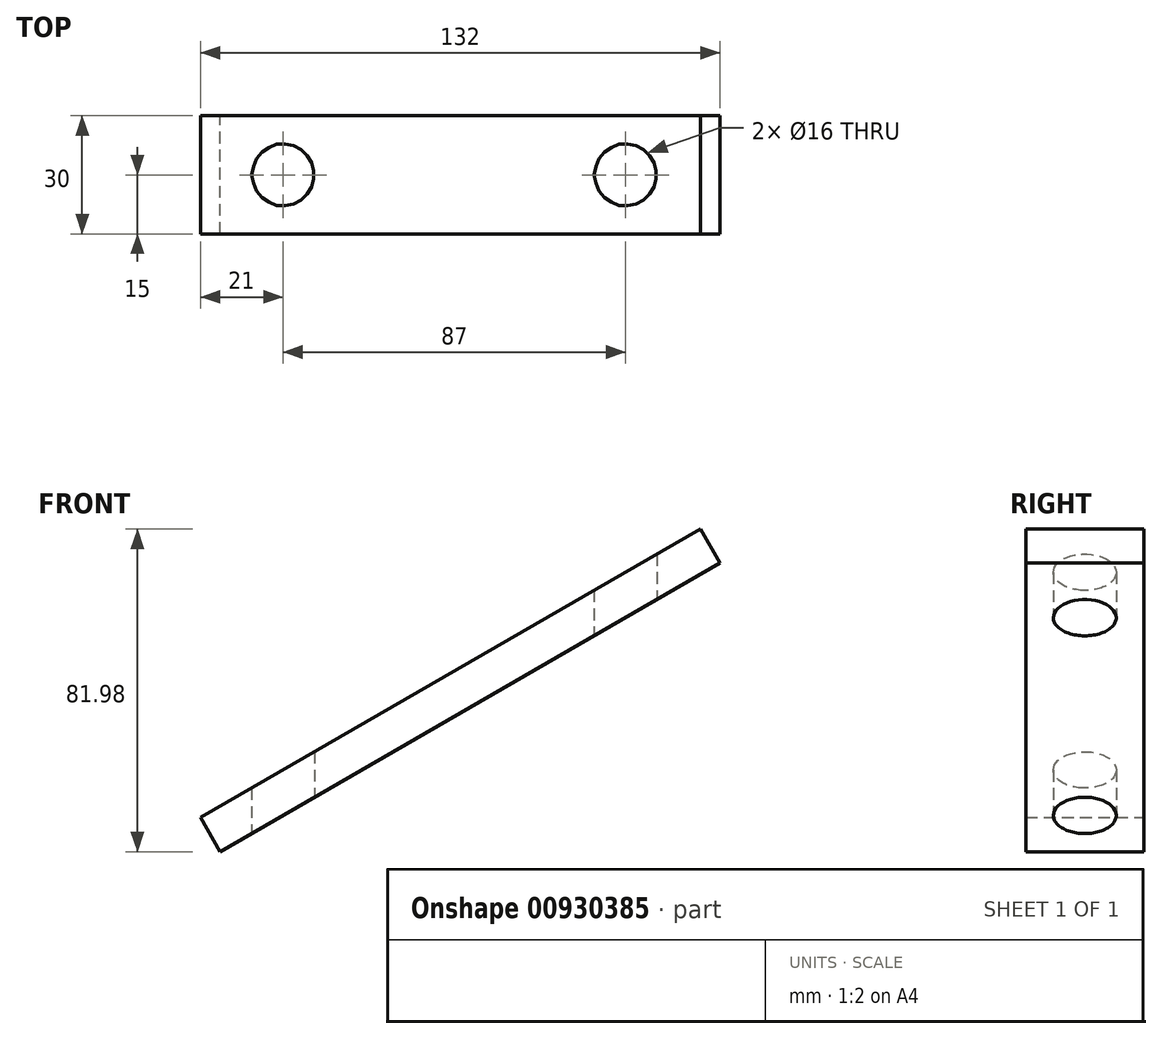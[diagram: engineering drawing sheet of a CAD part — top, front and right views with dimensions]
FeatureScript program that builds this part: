
annotation { "Feature Type Name" : "Feature", "Feature Type Description" : "" }
export const myFeature = defineFeature(function(context is Context, id is Id, definition is map)
    precondition{}
    {
        {
            var Q0;
            Q0=qCreatedBy(makeId("Top.planeOp"),FACE);
            var sketch = newSketch(context, id + "F0", { "sketchPlane" : qUnion([Q0])});
            skCircle(sketch, "E0", {"center": v(16, 0) * mm, "radius": 8 * mm});
            skCircle(sketch, "E1.1.0.0", {"center": v(103, 0) * mm, "radius": 8 * mm});
            skLineSegment(sketch, "E1.direction1", {"start": v(16, 0) * mm, "end": v(103, 0) * mm, "construction": true});
            skSolve(sketch);
        }
        {
            var Q0;
            Q0=qCreatedBy(makeId("Front.planeOp"),FACE);
            var sketch = newSketch(context, id + "F1", { "sketchPlane" : qUnion([Q0])});
            skLineSegment(sketch, "E2.bottom", {"start": v(-5, 8.66) * mm, "end": v(122, 81.98) * mm});
            skLineSegment(sketch, "E2.top", {"start": v(0, 0) * mm, "end": v(127, 73.32) * mm});
            skLineSegment(sketch, "E2.left", {"start": v(-5, 8.66) * mm, "end": v(0, 0) * mm});
            skLineSegment(sketch, "E2.right", {"start": v(122, 81.98) * mm, "end": v(127, 73.32) * mm});
            skLineSegment(sketch, "E3", {"start": v(103, 0) * mm, "end": v(103, 76.59) * mm, "construction": true});
            skSolve(sketch);
        }
        {
            var Q0;
            Q0 = qSketchRegion(id + "F1", true);
            extrude(context, id + "F2", {"entities" : qUnion([Q0]), "endBound" : BoundingType.SYMMETRIC, "depth" : 30 * mm, "offsetDistance" : 25 * mm});
        }
        {
            var Q0;
            Q0 = qSketchRegion(id + "F0", true);
            extrude(context, id + "F3", {"entities" : qUnion([Q0]), "operationType" : NewBodyOperationType.REMOVE, "endBound" : BoundingType.THROUGH_ALL, "depth" : 25 * mm, "offsetDistance" : 25 * mm});
        }
    });
